# Revit family: BC_Hitachi_Duct-LSP-RPIL_LOD400
name_source: partatom
category: Mechanical Equipment
revit_build: Autodesk Revit 2018 (Build: 20170223_1515(x64)
units: mm (PartAtom-declared; Revit-internal decimal feet)

## family parameters
Always vertical = Yes
Cut with Voids When Loaded = No
OmniClass Number = 23.75.10.00
OmniClass Title = Transformation and Conversion of Energy
Part Type = Normal
Room Calculation Point = No
Round Connector Dimension = Use Diameter
Shared = No
Work Plane-Based = No

## types (5) — shared parameters
BC_MODEL_ID = 513158
BC_OBJECT_ID = 207818
BC_OBJECT_VERSION = #3
Chute de Pression Evacuation = 0.0 Pa
Courant DC Maximal = 1 A
Description = Duct LSP (RPIL-FSRE)
Diamètre Etat Liquide  = 6 mm  [stored 0.019685 ft]
Diamètre Evacuation = 32 mm  [stored 0.104987 ft]
Diamètre Gaz = 13 mm  [stored 0.0426509 ft]
Fréquence = 50 Hz
Hauteur de Reprise = 134 mm
Hauteur de Soufflage = 126 mm  [stored 0.413386 ft]
Hauteur hors tout = 197 mm
Largeur de Reprise = 597 mm
Largeur de Soufflage = 478 mm  [stored 1.56824 ft]
Largeur hors tout = 750 mm  [stored 2.46063 ft]
Manufacturer = Hitachi Air Conditioning Europe SAS
MasterFormat = 23 73 00
Model = Duct LSP (RPIL-FSRE)
Nombres de Pôles  = 1
Omniclass = 23-33 25 00
Profondeur hors tout = 600 mm
Tension AC Min = 207 V
Tension AC max = 253 V
Tension Nominale = 230 V
Type de réfrigérant = R410A / R32
Uniformat = D3040

## per-type parameters (varying)
| type | BC_VARIANT_ID | Calibre d'Intensité | Capacité | Capacité de Chauffage Nominale | Capacité de Refroidissement Nominale | Courant Nominal | Courant d'usage | Débit Air Maximum | Niveau de pression acoustique max | Puissance AC Nominale | Puissance Acoustique Maximum | Puissance utile nominale |
| RPIL-0.4FSRE | 505517 | 0 A | 1100 W | 1300 W | 1100 W | 0 A | 0 A | 100.0 L/s | 24 | 40 W | 48 | 40 W |
| RPIL-0.6FSRE | 505518 | 1 A | 1700 W | 1900 W | 1700 W | 1 A | 1 A | 121.7 L/s | 27 | 50 W | 51 | 50 W |
| RPIL-0.8FSRE | 505519 | 1 A | 2200 W | 2500 W | 2200 W | 1 A | 1 A | 128.3 L/s | 28 | 50 W | 52 | 50 W |
| RPIL-1.0FSRE | 505520 | 1 A | 2800 W | 3200 W | 2800 W | 1 A | 1 A | 128.3 L/s | 28 | 50 W | 52 | 50 W |
| RPIL-1.5FSRE | 505521 | 1 A | 4000 W | 4800 W | 4000 W | 1 A | 1 A | 146.7 L/s | 30 | 50 W | 53 | 50 W |

note: column(s) folded — value = type name in every type: Référence, Type Comments

note: [stored X ft] marks values corroborated as IEEE doubles in the binary element streams (Revit-internal decimal feet)

## geometry (parser evidence)
native form markers: Blend x2
no freeform markers — native parametric forms only
